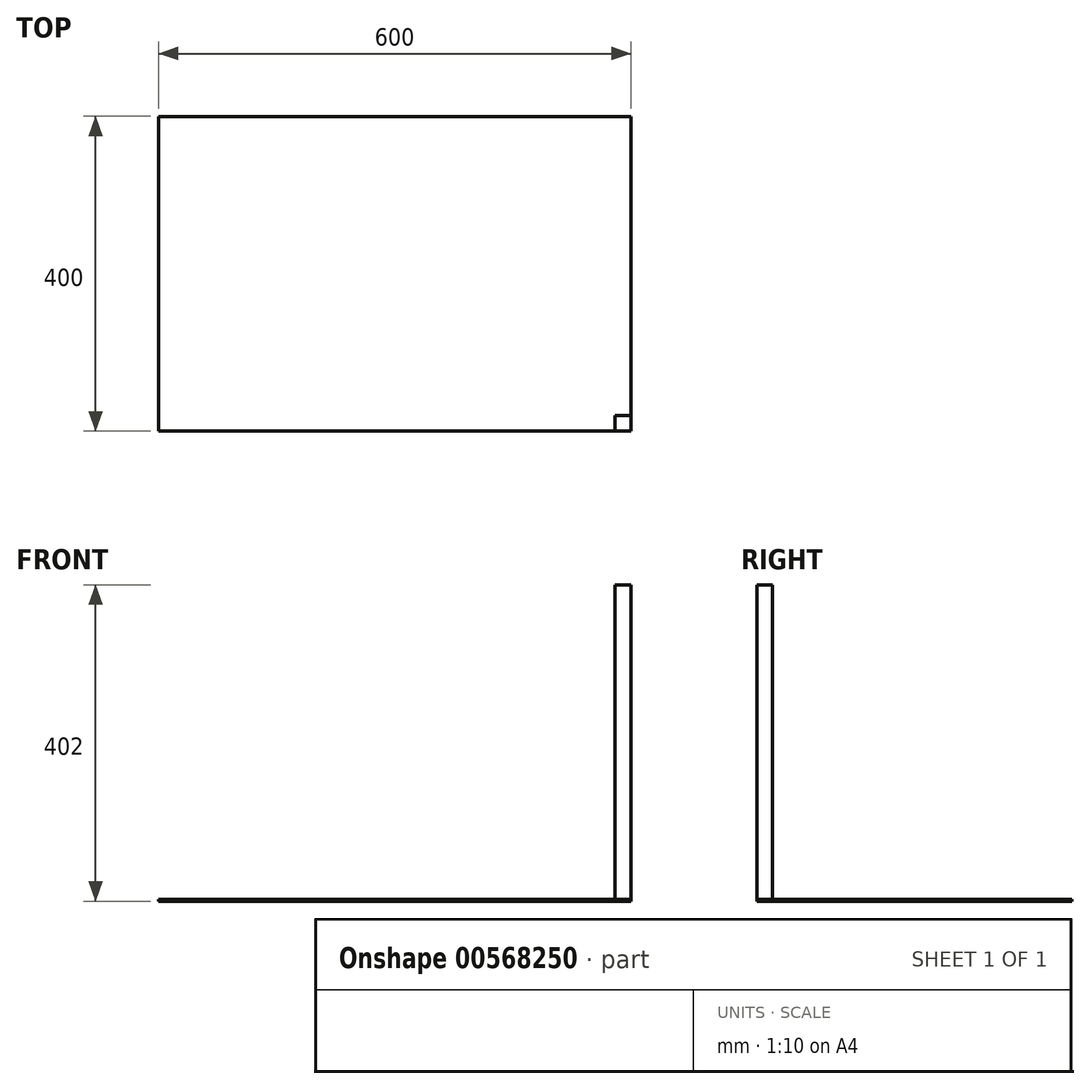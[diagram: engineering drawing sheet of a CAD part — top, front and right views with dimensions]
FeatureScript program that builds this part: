
annotation { "Feature Type Name" : "Feature", "Feature Type Description" : "" }
export const myFeature = defineFeature(function(context is Context, id is Id, definition is map)
    precondition{}
    {
        {
            var Q0;
            Q0=qCreatedBy(makeId("Top.planeOp"),FACE);
            var sketch = newSketch(context, id + "F0", { "sketchPlane" : qUnion([Q0])});
            skLineSegment(sketch, "E0.bottom", {"start": v(-348.07, 199.6) * mm, "end": v(251.93, 199.6) * mm});
            skLineSegment(sketch, "E0.top", {"start": v(-348.07, -200.4) * mm, "end": v(251.93, -200.4) * mm});
            skLineSegment(sketch, "E0.left", {"start": v(-348.07, 199.6) * mm, "end": v(-348.07, -200.4) * mm});
            skLineSegment(sketch, "E0.right", {"start": v(251.93, 199.6) * mm, "end": v(251.93, -200.4) * mm});
            skSolve(sketch);
        }
        {
            var Q0;
            Q0 = qSketchRegion(id + "F0", true);
            extrude(context, id + "F1", {"entities" : qUnion([Q0]), "depth" : 2 * mm, "offsetDistance" : 25 * mm});
        }
        {
            var Q0;
            Q0=makeQuery(id+"F1.opExtrude","CAP_FACE",FACE,{"disambiguationData":[OSD([sQuery(id+"F0.wireOp",EDGE,"E0.bottom"),sQuery(id+"F0.wireOp",EDGE,"E0.top"),sQuery(id+"F0.wireOp",EDGE,"E0.left"),sQuery(id+"F0.wireOp",EDGE,"E0.right")])],"isStart":false});
            var sketch = newSketch(context, id + "F2", { "sketchPlane" : qUnion([Q0])});
            skLineSegment(sketch, "E1.bottom", {"start": v(251.93, -200.4) * mm, "end": v(231.93, -200.4) * mm});
            skLineSegment(sketch, "E1.top", {"start": v(251.93, -180.4) * mm, "end": v(231.93, -180.4) * mm});
            skLineSegment(sketch, "E1.left", {"start": v(251.93, -200.4) * mm, "end": v(251.93, -180.4) * mm});
            skLineSegment(sketch, "E1.right", {"start": v(231.93, -200.4) * mm, "end": v(231.93, -180.4) * mm});
            skSolve(sketch);
        }
        {
            var Q0;
            Q0 = qSketchRegion(id + "F2", true);
            extrude(context, id + "F3", {"entities" : qUnion([Q0]), "depth" : 400 * mm, "offsetDistance" : 25 * mm});
        }
    });
